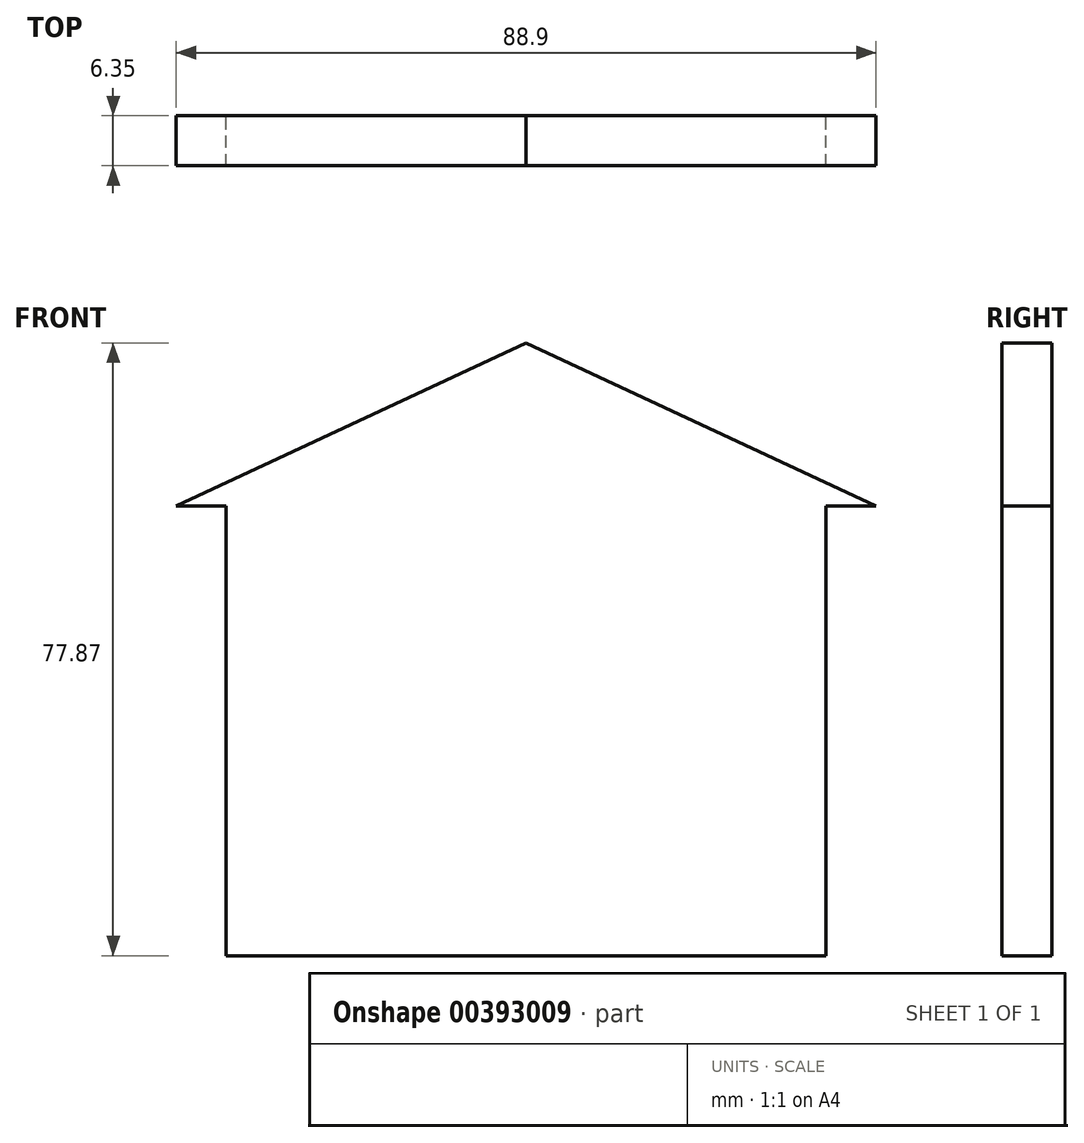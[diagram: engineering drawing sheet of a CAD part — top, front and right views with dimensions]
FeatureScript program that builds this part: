
annotation { "Feature Type Name" : "Feature", "Feature Type Description" : "" }
export const myFeature = defineFeature(function(context is Context, id is Id, definition is map)
    precondition{}
    {
        {
            var Q0;
            Q0=qCreatedBy(makeId("Front.planeOp"),FACE);
            var sketch = newSketch(context, id + "F0", { "sketchPlane" : qUnion([Q0])});
            skLineSegment(sketch, "E0.bottom", {"start": v(38.1, -28.57) * mm, "end": v(-38.1, -28.58) * mm});
            skLineSegment(sketch, "E0.left", {"start": v(38.1, -28.57) * mm, "end": v(38.1, 28.58) * mm});
            skLineSegment(sketch, "E0.right", {"start": v(-38.1, -28.58) * mm, "end": v(-38.1, 28.57) * mm});
            skPoint(sketch, "E0.middle", {"position": v(0, 0) * mm});
            skLineSegment(sketch, "E1", {"start": v(38.1, 28.58) * mm, "end": v(44.45, 28.58) * mm});
            skLineSegment(sketch, "E2", {"start": v(-38.1, 28.57) * mm, "end": v(-44.45, 28.57) * mm});
            skLineSegment(sketch, "E3", {"start": v(0, -28.58) * mm, "end": v(0, 49.3) * mm, "construction": true});
            skPoint(sketch, "E3.endSnap0", {"position": v(0, -28.58) * mm});
            skLineSegment(sketch, "E4", {"start": v(44.45, 28.58) * mm, "end": v(0, 49.3) * mm});
            skLineSegment(sketch, "E5", {"start": v(0, 49.3) * mm, "end": v(-44.45, 28.58) * mm});
            skSolve(sketch);
        }
        {
            var Q0;
            Q0 = qSketchRegion(id + "F0", true);
            extrude(context, id + "F1", {"entities" : qUnion([Q0]), "depth" : 6.35 * mm});
        }
    });
